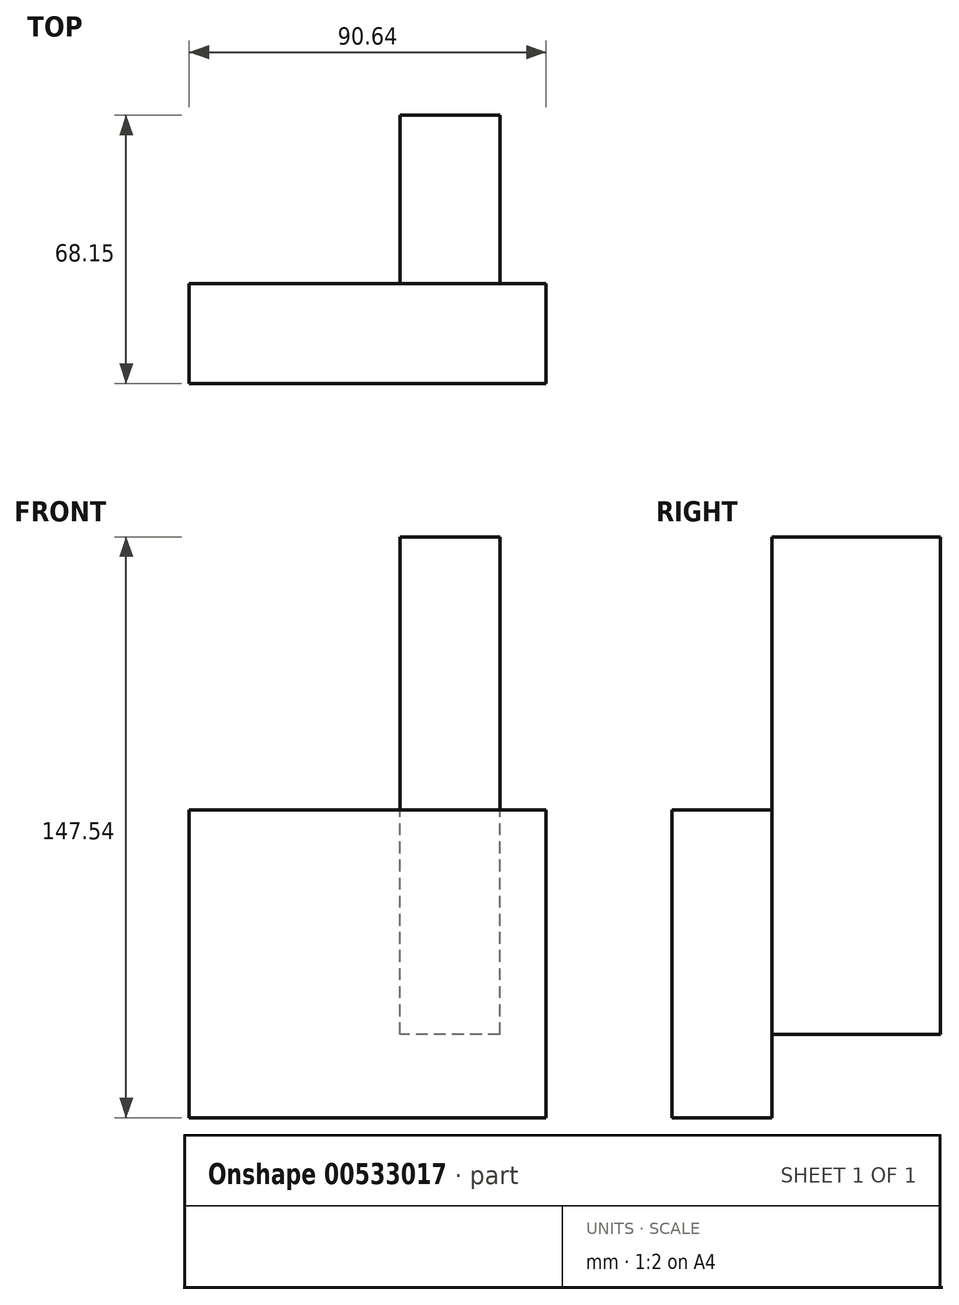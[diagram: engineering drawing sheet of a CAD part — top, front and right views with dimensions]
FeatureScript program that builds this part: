
annotation { "Feature Type Name" : "Feature", "Feature Type Description" : "" }
export const myFeature = defineFeature(function(context is Context, id is Id, definition is map)
    precondition{}
    {
        {
            var Q0;
            Q0=qCreatedBy(makeId("Front.planeOp"),FACE);
            var sketch = newSketch(context, id + "F0", { "sketchPlane" : qUnion([Q0])});
            skLineSegment(sketch, "E0.bottom", {"start": v(-53.55, 57.05) * mm, "end": v(37.09, 57.05) * mm});
            skLineSegment(sketch, "E0.top", {"start": v(-53.55, -21.17) * mm, "end": v(37.09, -21.17) * mm});
            skLineSegment(sketch, "E0.left", {"start": v(-53.55, 57.05) * mm, "end": v(-53.55, -21.17) * mm});
            skLineSegment(sketch, "E0.right", {"start": v(37.09, 57.05) * mm, "end": v(37.09, -21.17) * mm});
            skSolve(sketch);
        }
        {
            var Q0;
            Q0 = qSketchRegion(id + "F0", true);
            var sketch = newSketch(context, id + "F1", { "sketchPlane" : qUnion([Q0])});
            skSolve(sketch);
        }
        {
            var Q0;
            Q0=makeQuery(id+"F1.imprint","IMPRINT",FACE,{"disambiguationData":[TD([[makeQuery(id+"F1.imprint","IMPRINT",EDGE,{"derivedFrom":makeQuery(id+"F0.imprint","IMPRINT",EDGE,{"derivedFrom":sQuery(id+"F0.wireOp",EDGE,"E0.bottom")})}),-1.0]])]});
            extrude(context, id + "F2", {"entities" : qUnion([Q0]), "depth" : 25.4 * mm, "offsetDistance" : 25.4 * mm});
        }
        {
            var Q0;
            Q0=qCreatedBy(makeId("Right.planeOp"),FACE);
            var sketch = newSketch(context, id + "F3", { "sketchPlane" : qUnion([Q0])});
            skLineSegment(sketch, "E1.bottom", {"start": v(0, 0) * mm, "end": v(42.75, 0) * mm});
            skLineSegment(sketch, "E1.top", {"start": v(0, 126.37) * mm, "end": v(42.75, 126.37) * mm});
            skLineSegment(sketch, "E1.left", {"start": v(0, 0) * mm, "end": v(0, 126.37) * mm});
            skLineSegment(sketch, "E1.right", {"start": v(42.75, 0) * mm, "end": v(42.75, 126.37) * mm});
            skSolve(sketch);
        }
        {
            var Q0;
            Q0=makeQuery(id+"F3.imprint","IMPRINT",FACE,{"disambiguationData":[TD([[makeQuery(id+"F3.imprint","IMPRINT",EDGE,{"derivedFrom":sQuery(id+"F3.wireOp",EDGE,"E1.bottom")}),1.0]])]});
            extrude(context, id + "F4", {"entities" : qUnion([Q0]), "operationType" : NewBodyOperationType.ADD, "depth" : 25.4 * mm, "offsetDistance" : 25.4 * mm});
        }
    });
